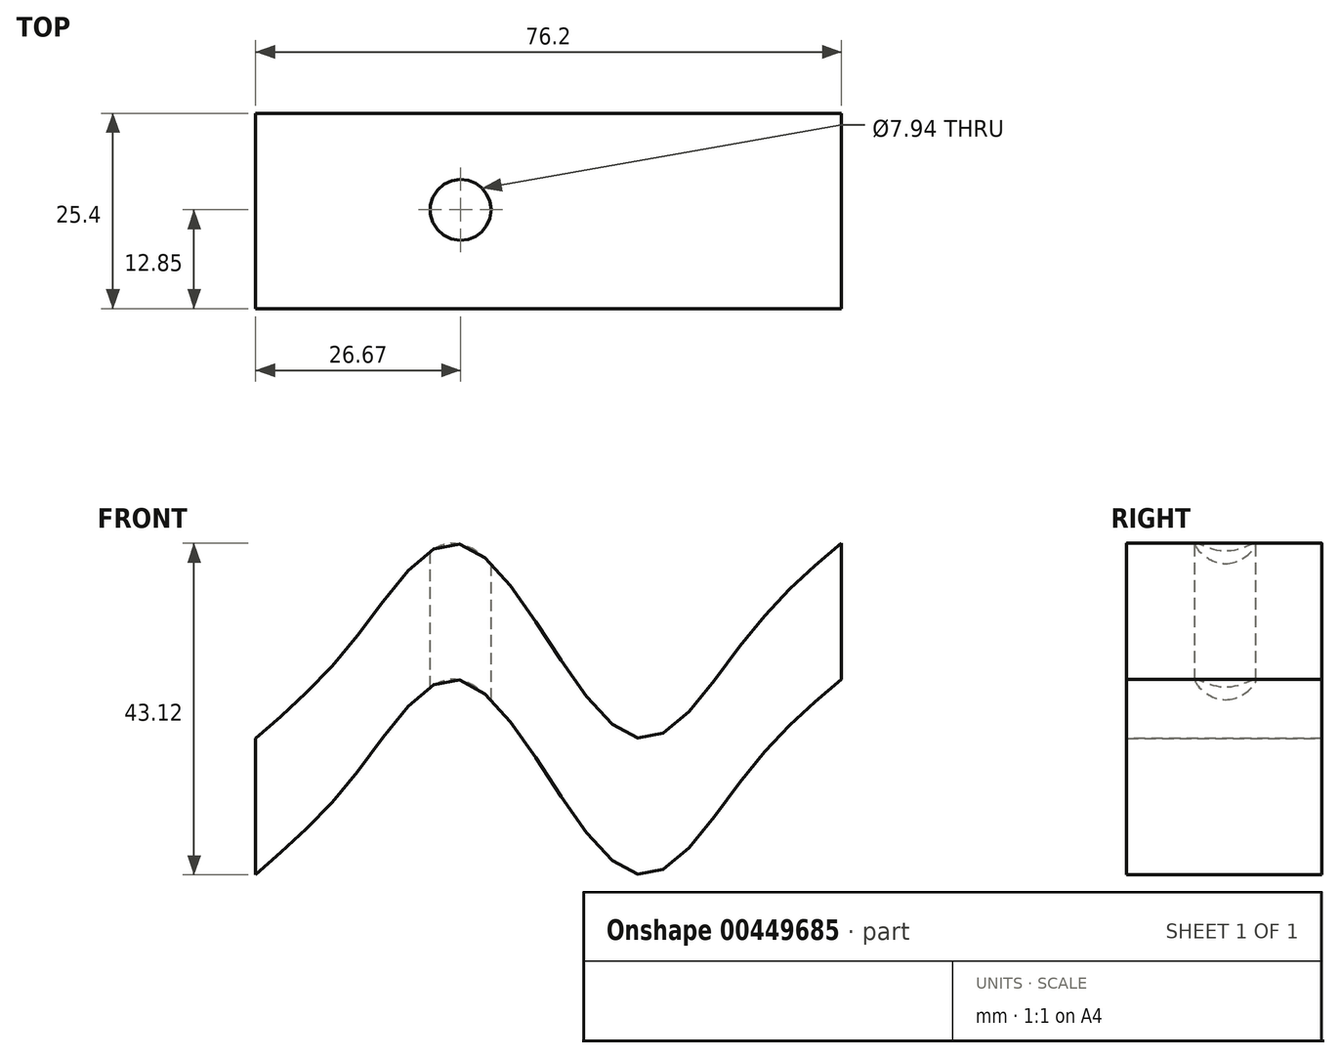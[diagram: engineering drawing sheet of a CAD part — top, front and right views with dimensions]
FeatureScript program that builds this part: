
annotation { "Feature Type Name" : "Feature", "Feature Type Description" : "" }
export const myFeature = defineFeature(function(context is Context, id is Id, definition is map)
    precondition{}
    {
        {
            var Q0;
            Q0=qCreatedBy(makeId("Front.planeOp"),FACE);
            var sketch = newSketch(context, id + "F0", { "sketchPlane" : qUnion([Q0])});
            skPoint(sketch, "E0", {"position": v(-38.1, -12.7) * mm});
            skPoint(sketch, "E1", {"position": v(-25.4, 0) * mm});
            skPoint(sketch, "E2", {"position": v(-12.7, 12.7) * mm});
            skPoint(sketch, "E3", {"position": v(0, 0) * mm});
            skPoint(sketch, "E4", {"position": v(12.7, -12.7) * mm});
            skPoint(sketch, "E5", {"position": v(25.4, 0) * mm});
            skPoint(sketch, "E6", {"position": v(38.1, 12.7) * mm});
            skFitSpline(sketch, "E7", {"points": [v(-38.1, -12.7) * mm, v(-25.4, 0) * mm, v(-12.7, 12.7) * mm, v(0, 0) * mm, v(12.7, -12.7) * mm, v(25.4, 0) * mm, v(38.1, 12.7) * mm], "startDerivative": vector(75.92, 66.04) * mm, "endDerivative": vector(80.78, 65.42) * mm});
            skPoint(sketch, "E8", {"position": v(-38.1, -30.4) * mm});
            skPoint(sketch, "E9", {"position": v(-25.4, -17.7) * mm});
            skPoint(sketch, "E10", {"position": v(-12.7, -5) * mm});
            skPoint(sketch, "E11", {"position": v(-20.35, -17.7) * mm});
            skPoint(sketch, "E12", {"position": v(12.7, -30.4) * mm});
            skPoint(sketch, "E13", {"position": v(25.4, -17.7) * mm});
            skPoint(sketch, "E14", {"position": v(38.1, -5) * mm});
            skFitSpline(sketch, "E15", {"points": [v(-38.1, -30.4) * mm, v(-25.4, -17.7) * mm, v(-12.7, -5) * mm, v(0, -17.7) * mm, v(12.7, -30.4) * mm, v(25.4, -17.7) * mm, v(38.1, -5) * mm], "startDerivative": vector(75.92, 66.04) * mm, "endDerivative": vector(80.78, 65.42) * mm});
            skLineSegment(sketch, "E16", {"start": v(-38.1, -30.4) * mm, "end": v(-38.1, -12.7) * mm});
            skLineSegment(sketch, "E17", {"start": v(38.1, 12.7) * mm, "end": v(38.1, -5) * mm});
            skSolve(sketch);
        }
        {
            var Q0;
            Q0 = qSketchRegion(id + "F0", true);
            extrude(context, id + "F1", {"entities" : qUnion([Q0]), "depth" : 25.4 * mm});
        }
        {
            var Q0;
            Q0=qCreatedBy(makeId("Top.planeOp"),FACE);
            var sketch = newSketch(context, id + "F2", { "sketchPlane" : qUnion([Q0])});
            skCircle(sketch, "E18", {"center": v(-11.43, -12.55) * mm, "radius": 3.97 * mm});
            skSolve(sketch);
        }
        {
            var Q0;
            Q0 = qSketchRegion(id + "F2", true);
            extrude(context, id + "F3", {"entities" : qUnion([Q0]), "operationType" : NewBodyOperationType.REMOVE, "endBound" : BoundingType.SYMMETRIC, "oppositeDirection" : true, "depth" : 51.82 * mm});
        }
    });
